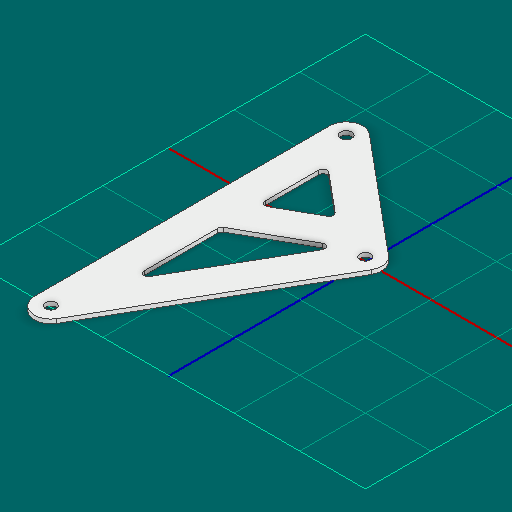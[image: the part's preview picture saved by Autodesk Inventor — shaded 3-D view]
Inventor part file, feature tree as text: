
AUTODESK INVENTOR PART (.ipt)
format: ipt  version: 2025 (Build 290162000, 162)  size: 142,848 bytes
history: native  units: in
note: dims shown in document units (in); Inventor stores cm internally (conversion verified against a paired STEP export)
features: other x3, extrude x1, sketch x1
ambient origin geometry x8: Origin, YZ Plane, XZ Plane, XY Plane, X Axis, Y Axis, Z Axis, Center Point
bodies: Solid1 (feature_tree)
feature tree (5):
  other  "Blocks"
  extrude  "Extrusion1"  Depth=0.5in
  sketch  "Sketch1"  dims[d1=0.5in d2=0.5in d3=0.5in d4=0.0625in d5=0.5in d6=0.0625in d7=0.0625in d8=0.0625in d9=0.0in d10=4.5in d12=0.5in d13=0.5in d14=0.5192in d16=1.75in d17=0.5in]
  other  "main"
  other  "main:1"
